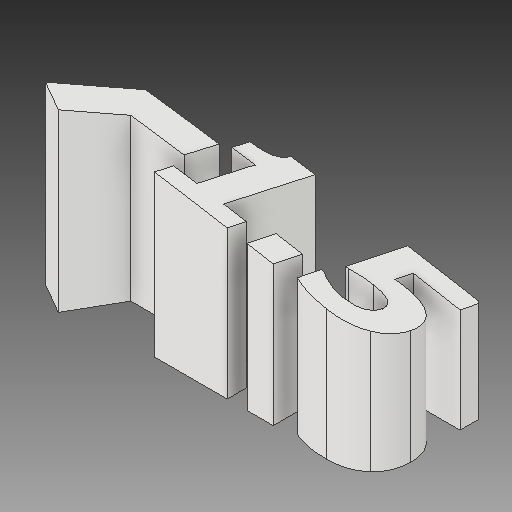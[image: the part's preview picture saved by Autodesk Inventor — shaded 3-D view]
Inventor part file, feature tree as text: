
AUTODESK INVENTOR PART (.ipt)
format: ipt  version: 2017 (Build 210142000, 142)  size: 232,448 bytes
history: native  units: in
note: dims shown in document units (in); Inventor stores cm internally (conversion verified against a paired STEP export)
features: sketch x2, reference x2, revolve x1, extrude x1, projected_geometry x1
ambient origin geometry x8: Origin, YZ Plane, XZ Plane, XY Plane, X Axis, Y Axis, Z Axis, Center Point
bodies: Solid1 (feature_tree)
feature tree (7):
  revolve  "Revolution1"  [1 undecoded]
  extrude  "Extrusion1"  Depth=0.075in
  sketch  "Sketch1"  dims[d0=0.8265in d1=0.175in]
  sketch  "Sketch2"  dims[d2=0.05in d3=0.1in d4=0.15in d5=0.275in d6=90.0deg d7=1.55in d16=0.6536in d31=0.035in d32=0.0175in d33=0.225in d34=0.1in d35=1.1in d36=0.035in d38=60.0deg d39=0.075in d40=0.0in d41=0.0in]
  projected_geometry  "Projected Loop1"
  reference  "Reference1"
  reference  "Reference2"
note: 1 required parameter value undecoded (feature->parameter linkage not recoverable at this tier; creation-order binding heuristic only, values carry confidence <= 0.55)
